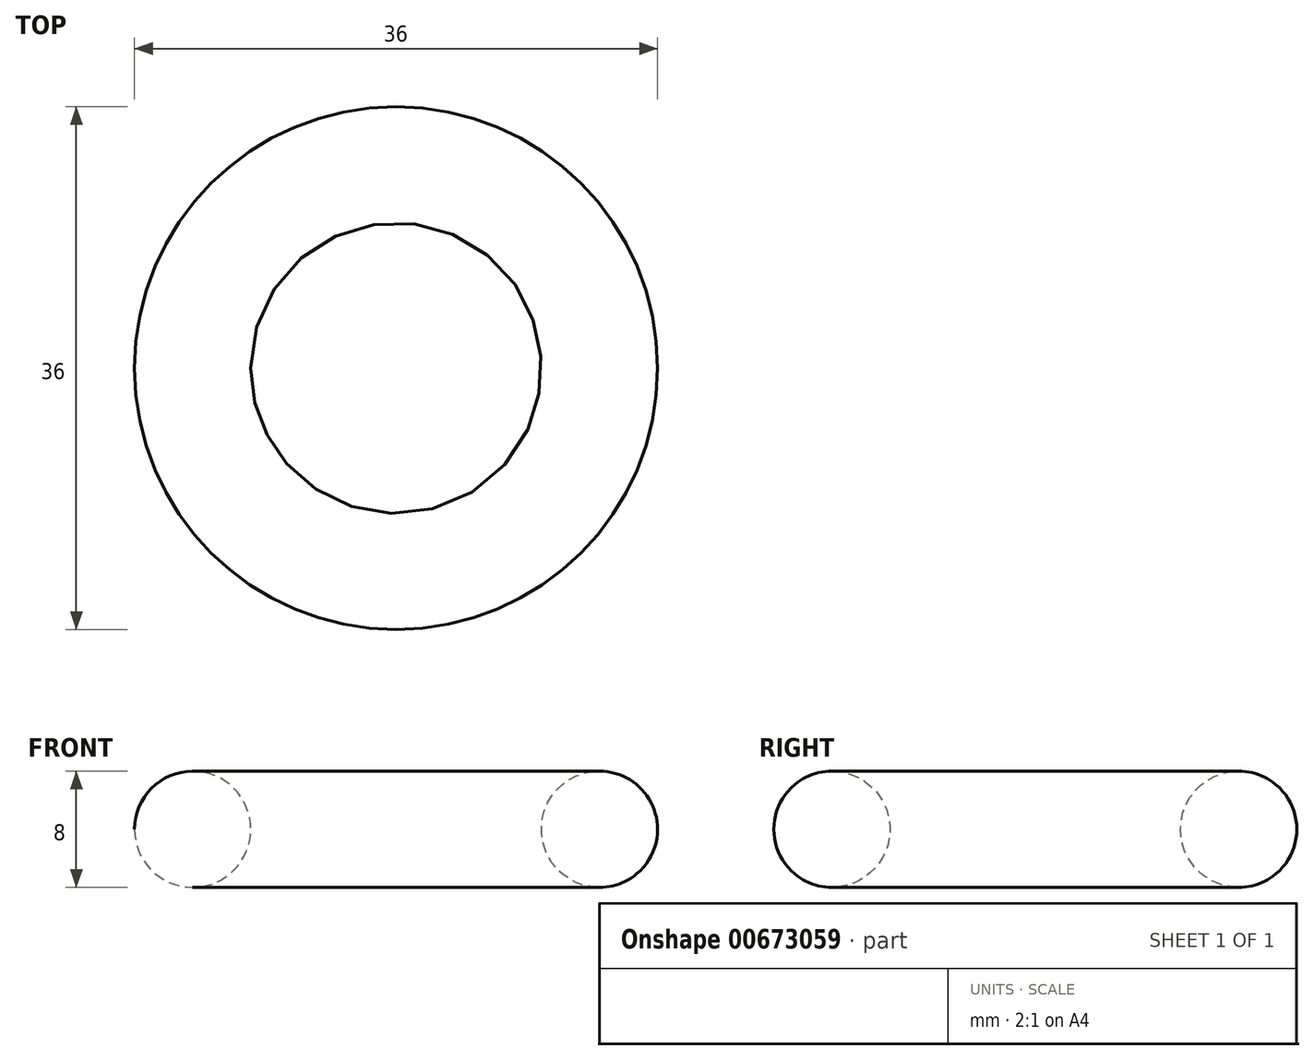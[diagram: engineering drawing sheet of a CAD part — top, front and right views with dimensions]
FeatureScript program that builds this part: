
annotation { "Feature Type Name" : "Feature", "Feature Type Description" : "" }
export const myFeature = defineFeature(function(context is Context, id is Id, definition is map)
    precondition{}
    {
        {
            var Q0;
            Q0=qCreatedBy(makeId("Front.planeOp"),FACE);
            var sketch = newSketch(context, id + "F0", { "sketchPlane" : qUnion([Q0])});
            skCircle(sketch, "E0", {"center": v(-14, 0) * mm, "radius": 4 * mm});
            skSolve(sketch);
        }
        {
            var Q0;
            Q0=qCreatedBy(makeId("Top.planeOp"),FACE);
            var sketch = newSketch(context, id + "F1", { "sketchPlane" : qUnion([Q0])});
            skCircle(sketch, "E1", {"center": v(0, 0) * mm, "radius": 14 * mm});
            skSolve(sketch);
        }
        {
            var Q0;
            Q0=makeQuery(id+"F0.imprint","IMPRINT",FACE,{"disambiguationData":[TD([[makeQuery(id+"F0.imprint","IMPRINT",EDGE,{"derivedFrom":sQuery(id+"F0.wireOp",EDGE,"E0")}),1.0]])]});
            var Q1;
            Q1=sQuery(id+"F1.wireOp",EDGE,"E1");
            revolve(context, id + "F2", {"surfaceOperationType" : NewSurfaceOperationType.NEW, "entities" : qUnion([Q0]), "axis" : qUnion([Q1]), "revolveType" : RevolveType.FULL});
        }
    });
